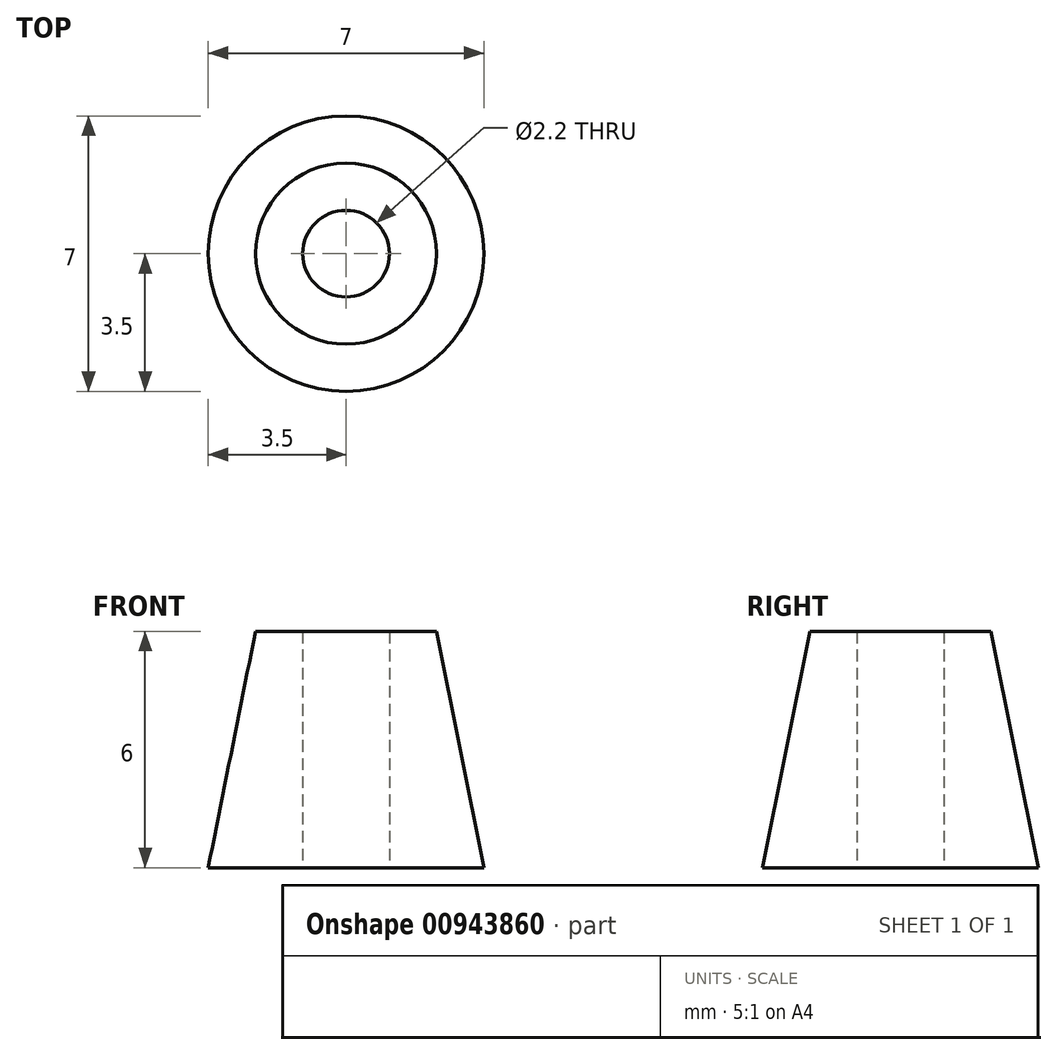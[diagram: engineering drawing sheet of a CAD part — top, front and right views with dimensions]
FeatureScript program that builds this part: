
annotation { "Feature Type Name" : "Feature", "Feature Type Description" : "" }
export const myFeature = defineFeature(function(context is Context, id is Id, definition is map)
    precondition{}
    {
        {
            var Q0;
            Q0=qCreatedBy(makeId("Front.planeOp"),FACE);
            var sketch = newSketch(context, id + "F0", { "sketchPlane" : qUnion([Q0])});
            skLineSegment(sketch, "E0", {"start": v(0, 0) * mm, "end": v(0, 1.3) * mm});
            skLineSegment(sketch, "E1", {"start": v(1.1, 6) * mm, "end": v(1.1, 0) * mm});
            skLineSegment(sketch, "E2", {"start": v(1.1, 0) * mm, "end": v(3.5, 0) * mm});
            skLineSegment(sketch, "E3", {"start": v(1.1, 6) * mm, "end": v(2.3, 6) * mm});
            skLineSegment(sketch, "E4", {"start": v(2.3, 6) * mm, "end": v(3.5, 0) * mm});
            skSolve(sketch);
        }
        {
            var Q0;
            Q0=makeQuery(id+"F0.imprint","IMPRINT",FACE,{"disambiguationData":[TD([[makeQuery(id+"F0.imprint","IMPRINT",EDGE,{"derivedFrom":sQuery(id+"F0.wireOp",EDGE,"E1")}),1.0]])]});
            var Q1;
            Q1=sQuery(id+"F0.wireOp",EDGE,"E0");
            revolve(context, id + "F1", {"surfaceOperationType" : NewSurfaceOperationType.NEW, "entities" : qUnion([Q0]), "axis" : qUnion([Q1]), "revolveType" : RevolveType.FULL});
        }
    });
